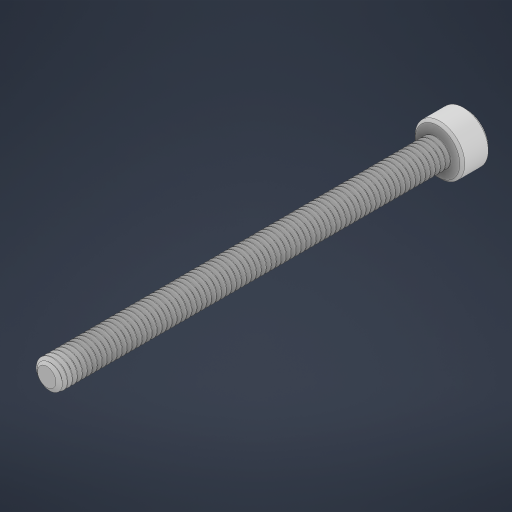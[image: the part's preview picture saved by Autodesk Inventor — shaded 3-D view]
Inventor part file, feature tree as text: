
AUTODESK INVENTOR PART (.ipt)
format: ipt  version: 2023 (Build 270158000, 158)  size: 2,024,960 bytes
history: native  units: in
note: dims shown in document units (in); Inventor stores cm internally (conversion verified against a paired STEP export)
features: chamfer x1
ambient origin geometry x8: Origin, YZ Plane, XZ Plane, XY Plane, X Axis, Y Axis, Z Axis, Center Point
bodies: Solid1 (feature_tree)
feature tree (1):
  chamfer  "Chamfer1"  [1 undecoded]
note: 1 required parameter value undecoded (feature->parameter linkage not recoverable at this tier; creation-order binding heuristic only, values carry confidence <= 0.55)
